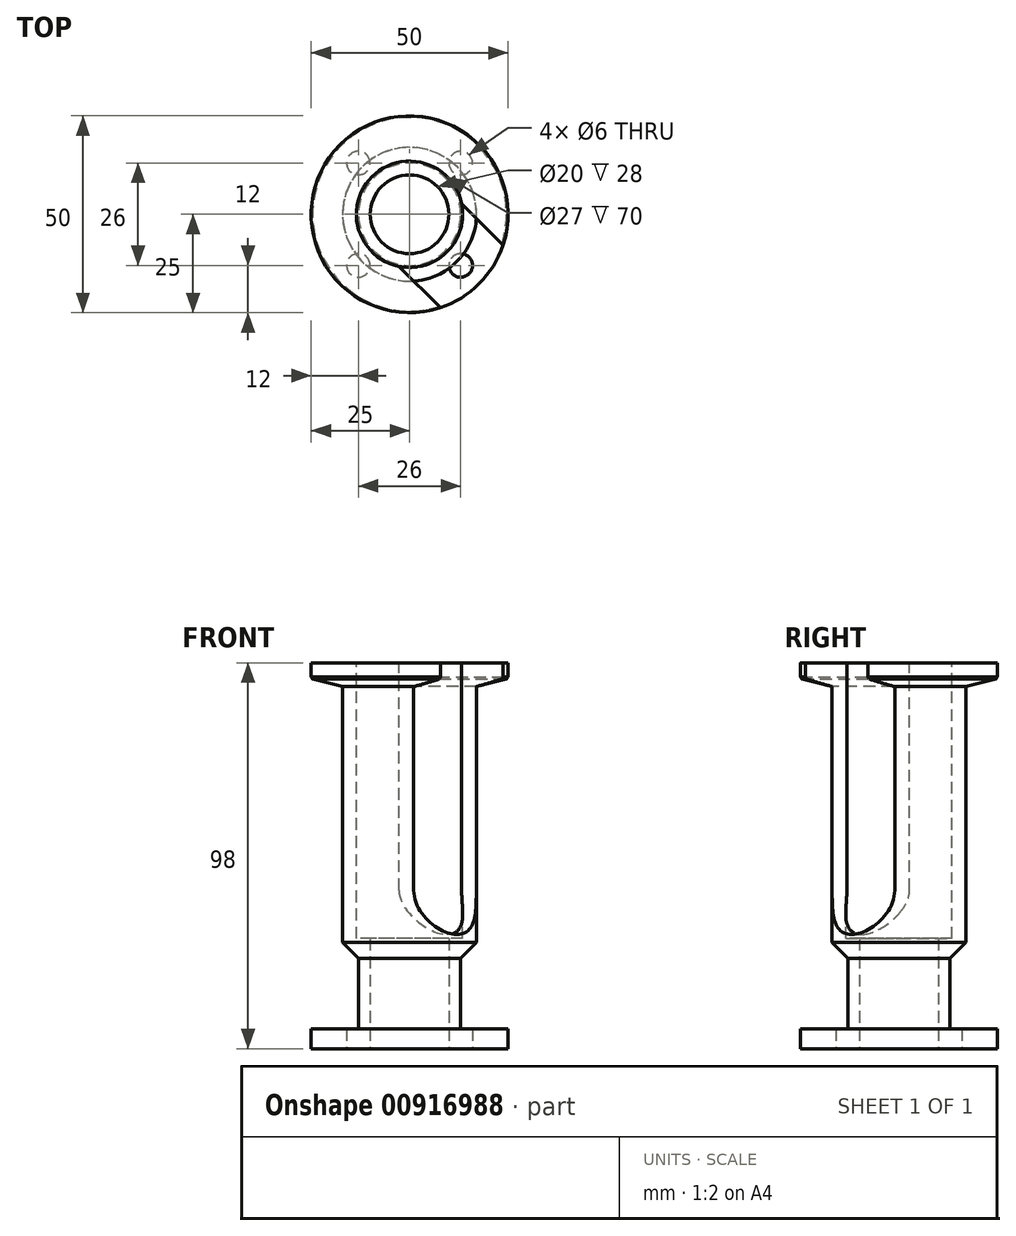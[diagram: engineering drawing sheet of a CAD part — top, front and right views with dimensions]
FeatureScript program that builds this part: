
annotation { "Feature Type Name" : "Feature", "Feature Type Description" : "" }
export const myFeature = defineFeature(function(context is Context, id is Id, definition is map)
    precondition{}
    {
        {
            var Q0;
            Q0=qCreatedBy(makeId("Top.planeOp"),FACE);
            var sketch = newSketch(context, id + "F0", { "sketchPlane" : qUnion([Q0])});
            skCircle(sketch, "E0", {"center": v(0, 0) * mm, "radius": 25 * mm});
            skCircle(sketch, "E1", {"center": v(0, 0) * mm, "radius": 10 * mm});
            skCircle(sketch, "E2", {"center": v(-13, 13) * mm, "radius": 3 * mm});
            skCircle(sketch, "E3.0.1.0", {"center": v(-13, -13) * mm, "radius": 3 * mm});
            skCircle(sketch, "E3.1.0.0", {"center": v(13, 13) * mm, "radius": 3 * mm});
            skCircle(sketch, "E3.1.1.0", {"center": v(13, -13) * mm, "radius": 3 * mm});
            skLineSegment(sketch, "E3.direction1", {"start": v(-13, 13) * mm, "end": v(13, 13) * mm, "construction": true});
            skLineSegment(sketch, "E3.direction2", {"start": v(-13, 13) * mm, "end": v(-13, -13) * mm, "construction": true});
            skSolve(sketch);
        }
        {
            var Q0;
            Q0=makeQuery(id+"F0.imprint","IMPRINT",FACE,{"disambiguationData":[TD([[makeQuery(id+"F0.imprint","IMPRINT",EDGE,{"derivedFrom":sQuery(id+"F0.wireOp",EDGE,"E0")}),1.0]])]});
            extrude(context, id + "F1", {"entities" : qUnion([Q0]), "depth" : 5 * mm, "offsetDistance" : 25 * mm});
        }
        {
            var Q0;
            Q0=makeQuery(id+"F1.opExtrude","CAP_FACE",FACE,{"disambiguationData":[OSD([sQuery(id+"F0.wireOp",EDGE,"E0"),sQuery(id+"F0.wireOp",EDGE,"E1"),sQuery(id+"F0.wireOp",EDGE,"E2"),sQuery(id+"F0.wireOp",EDGE,"E3.0.1.0"),sQuery(id+"F0.wireOp",EDGE,"E3.1.0.0"),sQuery(id+"F0.wireOp",EDGE,"E3.1.1.0")])],"isStart":false});
            var sketch = newSketch(context, id + "F2", { "sketchPlane" : qUnion([Q0])});
            skCircle(sketch, "E4", {"center": v(0, 0) * mm, "radius": 13 * mm});
            skCircle(sketch, "E5", {"center": v(0, 0) * mm, "radius": 10 * mm});
            skSolve(sketch);
        }
        {
            var Q0;
            Q0=makeQuery(id+"F2.imprint","IMPRINT",FACE,{"disambiguationData":[TD([[makeQuery(id+"F2.imprint","IMPRINT",EDGE,{"derivedFrom":sQuery(id+"F2.wireOp",EDGE,"E4")}),1.0]])]});
            extrude(context, id + "F3", {"entities" : qUnion([Q0]), "operationType" : NewBodyOperationType.ADD, "depth" : 18 * mm, "offsetDistance" : 25 * mm});
        }
        {
            var Q0;
            Q0=makeQuery(id+"F3.opExtrude","CAP_FACE",FACE,{"disambiguationData":[OSD([sQuery(id+"F2.wireOp",EDGE,"E4"),sQuery(id+"F2.wireOp",EDGE,"E5")])],"isStart":false});
            var sketch = newSketch(context, id + "F4", { "sketchPlane" : qUnion([Q0])});
            skCircle(sketch, "E6", {"center": v(0, 0) * mm, "radius": 17 * mm});
            skSolve(sketch);
        }
        {
            var Q0;
            Q0=makeQuery(id+"F4.imprint","IMPRINT",FACE,{"disambiguationData":[TD([[makeQuery(id+"F4.imprint","IMPRINT",EDGE,{"derivedFrom":sQuery(id+"F4.wireOp",EDGE,"E6")}),1.0]])]});
            var Q1;
            Q1=makeQuery(id+"F4.imprint","IMPRINT",FACE,{"disambiguationData":[TD([[makeQuery(id+"F4.imprint","IMPRINT",EDGE,{"derivedFrom":makeQuery(id+"F3.opExtrude","CAP_EDGE",EDGE,{"disambiguationData":[OSD([sQuery(id+"F2.wireOp",EDGE,"E4")])],"isStart":false})}),1.0]])]});
            var Q2;
            Q2=makeQuery(id+"F4.imprint","IMPRINT",FACE,{"disambiguationData":[TD([[makeQuery(id+"F4.imprint","IMPRINT",EDGE,{"derivedFrom":makeQuery(id+"F3.opExtrude","CAP_EDGE",EDGE,{"disambiguationData":[OSD([sQuery(id+"F2.wireOp",EDGE,"E5")])],"isStart":false})}),1.0]])]});
            extrude(context, id + "F5", {"entities" : qUnion([Q0, Q1, Q2]), "operationType" : NewBodyOperationType.ADD, "depth" : 75 * mm, "offsetDistance" : 25 * mm});
        }
        {
            var Q0;
            Q0=makeQuery(id+"F5.opExtrude","CAP_FACE",FACE,{"disambiguationData":[OSD([sQuery(id+"F4.wireOp",EDGE,"E6")])],"isStart":false});
            var sketch = newSketch(context, id + "F6", { "sketchPlane" : qUnion([Q0])});
            skCircle(sketch, "E7", {"center": v(0, 0) * mm, "radius": 25 * mm});
            skSolve(sketch);
        }
        {
            var Q0;
            Q0=makeQuery(id+"F6.imprint","IMPRINT",FACE,{"disambiguationData":[TD([[makeQuery(id+"F6.imprint","IMPRINT",EDGE,{"derivedFrom":sQuery(id+"F6.wireOp",EDGE,"E7")}),1.0]])]});
            var Q1;
            Q1=makeQuery(id+"F6.imprint","IMPRINT",FACE,{"disambiguationData":[TD([[makeQuery(id+"F6.imprint","IMPRINT",EDGE,{"derivedFrom":makeQuery(id+"F5.opExtrude","CAP_EDGE",EDGE,{"disambiguationData":[OSD([sQuery(id+"F4.wireOp",EDGE,"E6")])],"isStart":false})}),1.0]])]});
            extrude(context, id + "F7", {"entities" : qUnion([Q0, Q1]), "operationType" : NewBodyOperationType.ADD, "oppositeDirection" : true, "depth" : 6 * mm, "offsetDistance" : 25 * mm});
        }
        {
            var Q0;
            Q0=makeQuery(id+"F7.boolean.opBoolean","MERGE",FACE,{"derivedFrom":[makeQuery(id+"F5.opExtrude","CAP_FACE",FACE,{"disambiguationData":[OSD([sQuery(id+"F4.wireOp",EDGE,"E6")])],"isStart":false}),makeQuery(id+"F7.opExtrude","CAP_FACE",FACE,{"disambiguationData":[OSD([sQuery(id+"F6.wireOp",EDGE,"E7")])],"isStart":true})]});
            var sketch = newSketch(context, id + "F8", { "sketchPlane" : qUnion([Q0])});
            skCircle(sketch, "E8", {"center": v(0, 0) * mm, "radius": 13.5 * mm});
            skSolve(sketch);
        }
        {
            var Q0;
            Q0=makeQuery(id+"F8.imprint","IMPRINT",FACE,{"disambiguationData":[TD([[makeQuery(id+"F8.imprint","IMPRINT",EDGE,{"derivedFrom":sQuery(id+"F8.wireOp",EDGE,"E8")}),1.0]])]});
            extrude(context, id + "F9", {"entities" : qUnion([Q0]), "operationType" : NewBodyOperationType.REMOVE, "oppositeDirection" : true, "depth" : 70 * mm, "offsetDistance" : 25 * mm});
        }
        {
            var Q0;
            Q0=makeQuery(id+"F5.boolean.opBoolean","SPLIT",FACE,{"disambiguationData":[TD([makeQuery(id+"F1.opExtrude","SWEPT_FACE",FACE,{"disambiguationData":[OSD([sQuery(id+"F0.wireOp",EDGE,"E1")])]})])],"derivedFrom":makeQuery(id+"F5.opExtrude","CAP_FACE",FACE,{"disambiguationData":[OSD([sQuery(id+"F4.wireOp",EDGE,"E6")])],"isStart":true})});
            var sketch = newSketch(context, id + "F10", { "sketchPlane" : qUnion([Q0])});
            skCircle(sketch, "E9", {"center": v(0, 0) * mm, "radius": 10 * mm});
            skSolve(sketch);
        }
        {
            var Q0;
            Q0=makeQuery(id+"F10.imprint","IMPRINT",FACE,{"disambiguationData":[TD([[makeQuery(id+"F10.imprint","IMPRINT",EDGE,{"derivedFrom":sQuery(id+"F10.wireOp",EDGE,"E9")}),-1.0]])]});
            extrude(context, id + "F11", {"entities" : qUnion([Q0]), "operationType" : NewBodyOperationType.REMOVE, "endBound" : BoundingType.THROUGH_ALL, "oppositeDirection" : true, "depth" : 25 * mm, "offsetDistance" : 25 * mm});
        }
        {
            var Q0;
            Q0=qCreatedBy(makeId("Front.planeOp"),FACE);
            var sketch = newSketch(context, id + "F12", { "sketchPlane" : qUnion([Q0])});
            skLineSegment(sketch, "E10", {"start": v(0, 0) * mm, "end": v(0, 93.44) * mm, "construction": true});
            skSolve(sketch);
        }
        {
            var Q0;
            Q0=qCreatedBy(makeId("Front.planeOp"),FACE);
            var Q1;
            Q1=sQuery(id+"F12.wireOp",EDGE,"E10");
            cPlane(context, id + "F13", {"entities" : qUnion([Q0, Q1]), "cplaneType" : CPlaneType.LINE_ANGLE, "offset" : 25 * mm, "angle" : 45 * degree, "width" : 150 * mm, "height" : 150 * mm});
        }
        {
            var Q0;
            Q0=qCreatedBy(id+"F13.planeOp",FACE);
            var sketch = newSketch(context, id + "F14", { "sketchPlane" : qUnion([Q0])});
            skArc(sketch, "E11", {"start": v(-11.25, 98.07) * mm, "mid": v(-11.25, 98) * mm, "end": v(-11.25, 97.93) * mm});
            skArc(sketch, "E12", {"start": v(-11.25, 40.25) * mm, "mid": v(0, 29) * mm, "end": v(11.25, 40.25) * mm});
            skLineSegment(sketch, "E13", {"start": v(11.25, 40.25) * mm, "end": v(11.25, 98) * mm});
            skLineSegment(sketch, "E14", {"start": v(-11.25, 98.07) * mm, "end": v(-11.25, 40.25) * mm});
            skLineSegment(sketch, "E15", {"start": v(11.25, 98) * mm, "end": v(-11.25, 98.07) * mm});
            skSolve(sketch);
        }
        {
            var Q0;
            {var subQ0=sQuery(id+"F14.wireOp",EDGE,"E12");Q0=makeQuery(id+"F14.imprint","IMPRINT",FACE,{"disambiguationData":[TD([[makeQuery(id+"F14.imprint","IMPRINT",EDGE,{"derivedFrom":subQ0}),1.0]])]});}
            extrude(context, id + "F15", {"entities" : qUnion([Q0]), "operationType" : NewBodyOperationType.REMOVE, "oppositeDirection" : true, "depth" : 25 * mm, "offsetDistance" : 25 * mm});
        }
        {
            var Q0;
            Q0=makeQuery(id+"F5.opExtrude","CAP_EDGE",EDGE,{"disambiguationData":[OSD([sQuery(id+"F4.wireOp",EDGE,"E6")])],"isStart":true});
            chamfer(context, id + "F16", {"entities" : qUnion([Q0]), "width" : 4 * mm, "tangentPropagation" : true});
        }
        {
            var Q0;
            Q0=makeQuery(id+"F7.opExtrude","CAP_EDGE",EDGE,{"disambiguationData":[OSD([sQuery(id+"F6.wireOp",EDGE,"E7")])],"isStart":false});
            chamfer(context, id + "F17", {"entities" : qUnion([Q0]), "chamferType" : ChamferType.TWO_OFFSETS, "width1" : 2 * mm, "oppositeDirection" : false, "width2" : 8 * mm, "tangentPropagation" : true});
        }
        {
            var Q0;
            {var subQ0=sQuery(id+"F6.wireOp",EDGE,"E7");Q0=makeQuery(id+"F17.opChamfer","BLEND_EDGE",EDGE,{"blendedFrom":[makeQuery(id+"F7.opExtrude","CAP_EDGE",EDGE,{"disambiguationData":[OSD([subQ0])],"isStart":false}),makeQuery(id+"F7.opExtrude","SWEPT_FACE",FACE,{"disambiguationData":[OSD([subQ0])]})],"blendedInto":[makeQuery(id+"F7.opExtrude","SWEPT_FACE",FACE,{"disambiguationData":[OSD([subQ0])]})]});}
            chamfer(context, id + "F18", {"entities" : qUnion([Q0]), "width" : .5 * mm, "tangentPropagation" : true});
        }
    });
